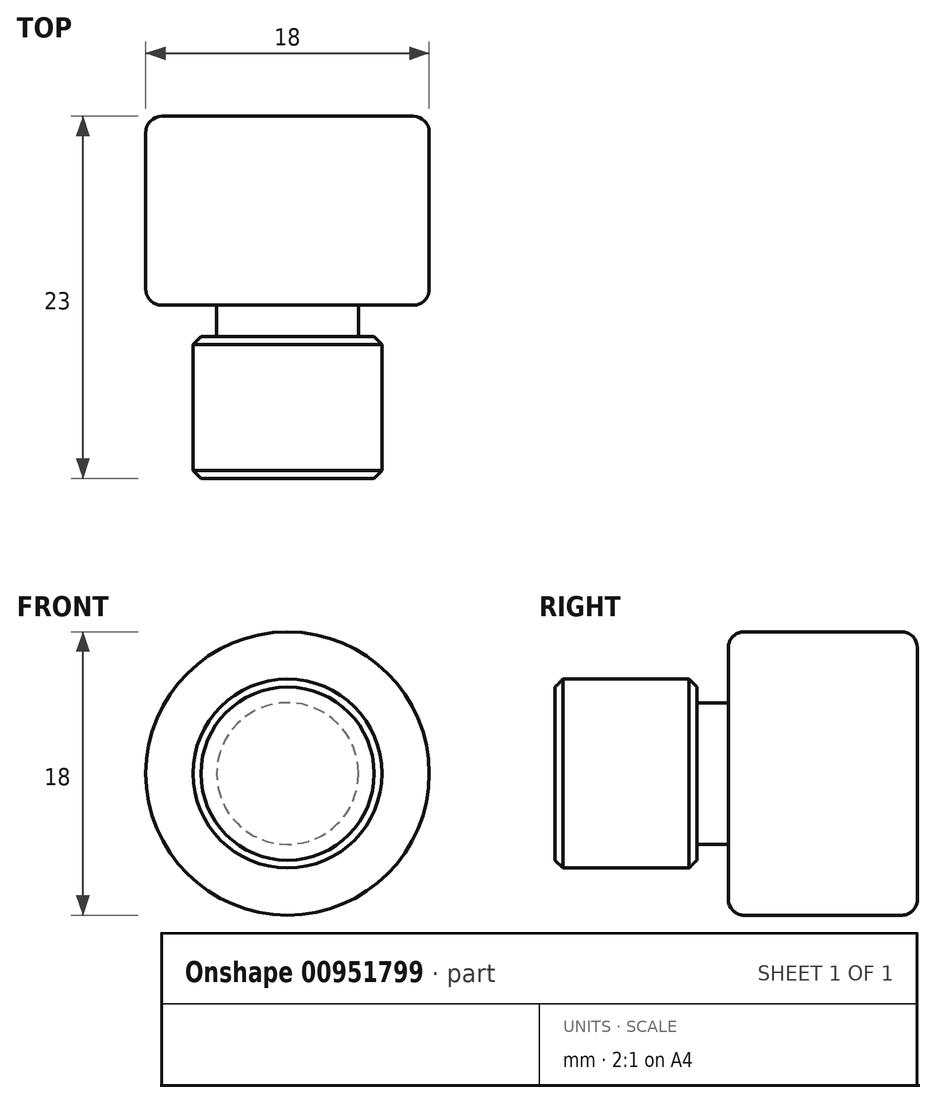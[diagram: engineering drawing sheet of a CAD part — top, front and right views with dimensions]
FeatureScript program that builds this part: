
annotation { "Feature Type Name" : "Feature", "Feature Type Description" : "" }
export const myFeature = defineFeature(function(context is Context, id is Id, definition is map)
    precondition{}
    {
        {
            var Q0;
            Q0=qCreatedBy(makeId("Right.planeOp"),FACE);
            var sketch = newSketch(context, id + "F0", { "sketchPlane" : qUnion([Q0])});
            skLineSegment(sketch, "E0", {"start": v(0, 0) * mm, "end": v(0, 6) * mm});
            skLineSegment(sketch, "E1", {"start": v(0, 6) * mm, "end": v(9, 6) * mm});
            skLineSegment(sketch, "E2", {"start": v(9, 6) * mm, "end": v(9, 4.5) * mm});
            skLineSegment(sketch, "E3", {"start": v(9, 4.5) * mm, "end": v(11, 4.5) * mm});
            skLineSegment(sketch, "E4", {"start": v(11, 4.5) * mm, "end": v(11, 9) * mm});
            skLineSegment(sketch, "E5", {"start": v(11, 9) * mm, "end": v(23, 9) * mm});
            skLineSegment(sketch, "E6", {"start": v(23, 9) * mm, "end": v(23, 0) * mm});
            skLineSegment(sketch, "E7", {"start": v(23, 0) * mm, "end": v(0, 0) * mm});
            skSolve(sketch);
        }
        {
            var Q0;
            Q0=makeQuery(id+"F0.imprint","IMPRINT",FACE,{"disambiguationData":[TD([[makeQuery(id+"F0.imprint","IMPRINT",EDGE,{"derivedFrom":sQuery(id+"F0.wireOp",EDGE,"E0")}),-1.0]])]});
            var Q1;
            Q1=sQuery(id+"F0.wireOp",EDGE,"E7");
            revolve(context, id + "F1", {"surfaceOperationType" : NewSurfaceOperationType.NEW, "entities" : qUnion([Q0]), "axis" : qUnion([Q1]), "revolveType" : RevolveType.FULL});
        }
        {
            var Q0;
            Q0=makeQuery(id+"F1.opRevolve","SWEPT_EDGE",EDGE,{"disambiguationData":[OSD([sQuery(id+"F0.wireOp",EDGE,"E0"),sQuery(id+"F0.wireOp",EDGE,"E1")])]});
            var Q1;
            Q1=makeQuery(id+"F1.opRevolve","SWEPT_EDGE",EDGE,{"disambiguationData":[OSD([sQuery(id+"F0.wireOp",EDGE,"E1"),sQuery(id+"F0.wireOp",EDGE,"E2")])]});
            chamfer(context, id + "F2", {"entities" : qUnion([Q0, Q1]), "width" : 0.5 * mm, "tangentPropagation" : true});
        }
        {
            var Q0;
            Q0=makeQuery(id+"F1.opRevolve","SWEPT_EDGE",EDGE,{"disambiguationData":[OSD([sQuery(id+"F0.wireOp",EDGE,"E4"),sQuery(id+"F0.wireOp",EDGE,"E5")])]});
            var Q1;
            Q1=makeQuery(id+"F1.opRevolve","SWEPT_EDGE",EDGE,{"disambiguationData":[OSD([sQuery(id+"F0.wireOp",EDGE,"E5"),sQuery(id+"F0.wireOp",EDGE,"E6")])]});
            fillet(context, id + "F3", {"entities" : qUnion([Q0, Q1]), "radius" : 1 * mm, "tangentPropagation" : true, "allowEdgeOverflow" : false});
        }
    });
